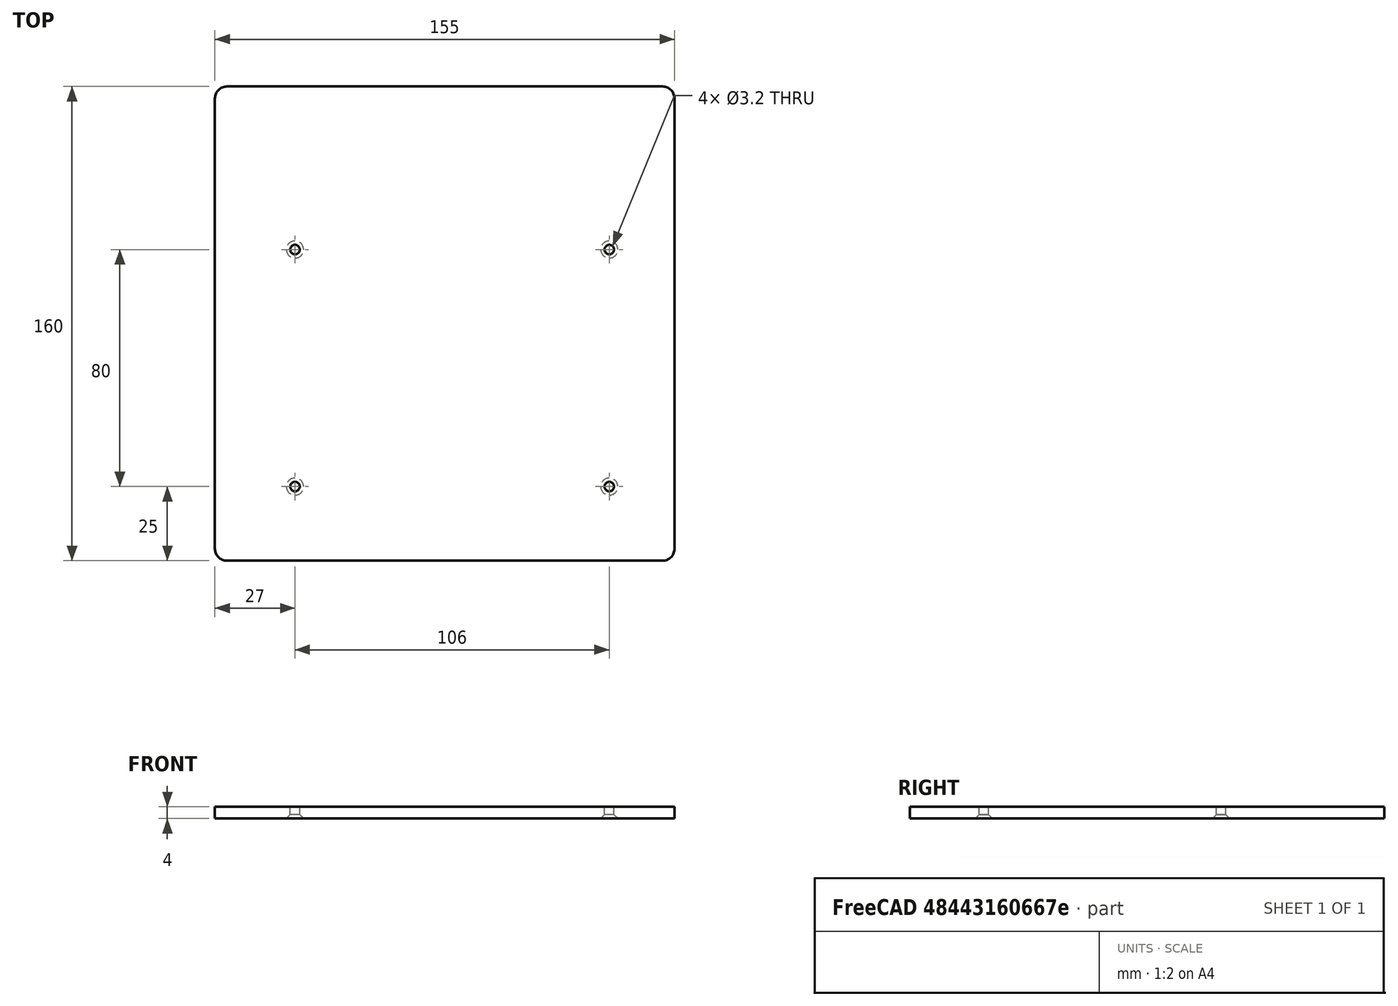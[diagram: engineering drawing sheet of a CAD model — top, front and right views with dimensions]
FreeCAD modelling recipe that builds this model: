
FCSTD DOCUMENT  (FreeCAD 0.17R11509 (Git))
Label: plate
License: All rights reserved
LicenseURL: http://en.wikipedia.org/wiki/All_rights_reserved
objects: Part::Cut×5, Part::Cone×4, Part::Cylinder×4, Mesh::Feature×1, Sketcher::SketchObject×1, PartDesign::Pad×1, Part::MultiFuse×1
note: 17 computed .brp shape members not serialized (recipe doc carries the construction recipe); baked Part::Feature solids carry a one-line shape summary decoded from their .brp

FEATURE [Part::Cone] Cone  label="cone"
  Angle = 360
  AttacherType = Attacher::AttachEngine3D
  Height = 2
  Placement = pos=(55.5,-55,-0.1) rot=(0,0,1;0rad)
  Radius1 = 3
  Radius2 = 1
FEATURE [Part::Cone] Cone001
  Angle = 360
  AttacherType = Attacher::AttachEngine3D
  Height = 2
  Placement = pos=(55.5,25,-0.1) rot=(0,0,1;0rad)
  Radius1 = 3
  Radius2 = 1
FEATURE [Part::Cone] Cone002
  Angle = 360
  AttacherType = Attacher::AttachEngine3D
  Height = 2
  Placement = pos=(-50.5,25,-0.1) rot=(0,0,1;0rad)
  Radius1 = 3
  Radius2 = 1
FEATURE [Part::Cone] Cone003
  Angle = 360
  AttacherType = Attacher::AttachEngine3D
  Height = 2
  Placement = pos=(-50.5,-55,-0.1) rot=(0,0,1;0rad)
  Radius1 = 3
  Radius2 = 1
FEATURE [Mesh::Feature] tronxy_plate_1  label="tronxy-plate_1"
  Placement = pos=(2.5,0,0) rot=(0,0,1;0rad)
FEATURE [Sketcher::SketchObject] Sketch
  MapMode = 5
  sketch-geometry (8):
    g0: LineSegment StartX=-77.5 StartY=76 StartZ=0 EndX=-77.5 EndY=-76 EndZ=0
    g1: LineSegment StartX=77.5 StartY=76 StartZ=0 EndX=77.5 EndY=-76 EndZ=0
    g2: ArcOfCircle CenterX=-73.5 CenterY=76 CenterZ=0 NormalX=0 NormalY=0 NormalZ=1 Radius=4 StartAngle=1.5708 EndAngle=3.14159
    g3: ArcOfCircle CenterX=73.5 CenterY=76 CenterZ=0 NormalX=0 NormalY=0 NormalZ=1 Radius=4 StartAngle=0 EndAngle=1.5708
    g4: ArcOfCircle CenterX=73.5 CenterY=-76 CenterZ=0 NormalX=0 NormalY=0 NormalZ=1 Radius=4 StartAngle=4.71239 EndAngle=6.28319
    g5: ArcOfCircle CenterX=-73.5 CenterY=-76 CenterZ=0 NormalX=0 NormalY=0 NormalZ=1 Radius=4 StartAngle=3.14159 EndAngle=4.71239
    g6: LineSegment StartX=-73.5 StartY=-80 StartZ=0 EndX=73.5 EndY=-80 EndZ=0
    g7: LineSegment StartX=73.5 StartY=80 StartZ=0 EndX=-73.5 EndY=80 EndZ=0
  constraints (28):
    c: Vertical(g0)
    c: Vertical(g1)
    c: Coincident(g2,g0)
    c: Coincident(g3,g1)
    c: Coincident(g4,g1)
    c: Coincident(g5,g0)
    c: Coincident(g6,g5)
    c: Coincident(g6,g4)
    c: Horizontal(g6)
    c: Tangent(g6,g5)
    c: Coincident(g7,g3)
    c: Coincident(g7,g2)
    c: Tangent(g4,g6,g4) = -1.5708
    c: Tangent(g5,g0,g0) = -1.5708
    c: Tangent(g0,g2,g0) = -1.5708
    c: Tangent(g2,g7,g2) = -1.5708
    c: Tangent(g7,g3,g3) = -1.5708
    c: Tangent(g3,g1,g1) = 1.5708
    c: Tangent(g1,g4,g1) = 1.5708
    c: Horizontal(g7)
    c: Equal(g4,g3)
    c: Equal(g3,g5)
    c: Equal(g5,g2)
    c: Radius(g2) = 4
    c: DistanceX(g2) = -73.5
    c: DistanceY(g2) = 76
    c: DistanceX(g4) = 73.5
    c: DistanceY(g4) = -76
FEATURE [PartDesign::Pad] Pad
  Length = 4
  Length2 = 100
  Profile = -> Sketch
  Type = 0
FEATURE [Part::Cut] Cut
  Base = -> Pad
  Tool = -> Cone
FEATURE [Part::Cut] Cut001
  Base = -> Cut
  Tool = -> Cone001
FEATURE [Part::Cut] Cut002
  Base = -> Cut001
  Tool = -> Cone002
FEATURE [Part::Cut] Cut003
  Base = -> Cut002
  Tool = -> Cone003
FEATURE [Part::Cylinder] Cylinder
  Angle = 360
  AttacherType = Attacher::AttachEngine3D
  Height = 10
  Placement = pos=(-50.5,25,-1) rot=(0,0,1;0rad)
  Radius = 1.6
FEATURE [Part::Cylinder] Cylinder001
  Angle = 360
  AttacherType = Attacher::AttachEngine3D
  Height = 10
  Placement = pos=(55.5,25,-1) rot=(0,0,1;0rad)
  Radius = 1.6
FEATURE [Part::Cylinder] Cylinder002
  Angle = 360
  AttacherType = Attacher::AttachEngine3D
  Height = 10
  Placement = pos=(55.5,-55,-1) rot=(0,0,1;0rad)
  Radius = 1.6
FEATURE [Part::Cylinder] Cylinder003
  Angle = 360
  AttacherType = Attacher::AttachEngine3D
  Height = 10
  Placement = pos=(-50.5,-55,-1) rot=(0,0,1;0rad)
  Radius = 1.6
FEATURE [Part::MultiFuse] Fusion
  Shapes = -> [Cylinder,Cylinder001,Cylinder003,Cylinder002]
FEATURE [Part::Cut] Cut004
  Base = -> Cut003
  Tool = -> Fusion
